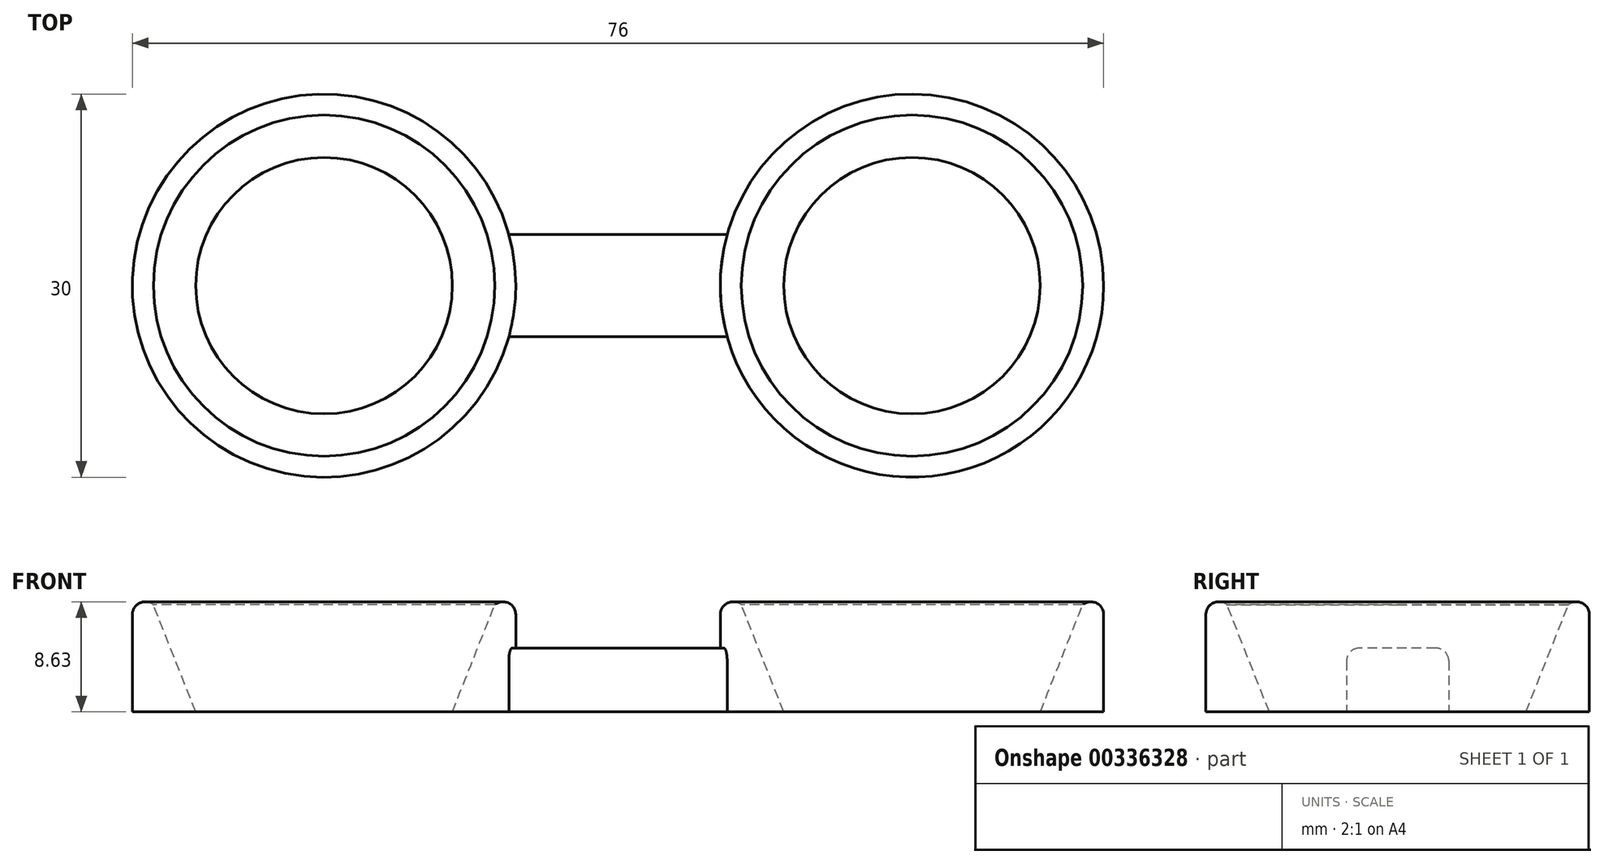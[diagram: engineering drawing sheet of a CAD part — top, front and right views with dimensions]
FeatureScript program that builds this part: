
annotation { "Feature Type Name" : "Feature", "Feature Type Description" : "" }
export const myFeature = defineFeature(function(context is Context, id is Id, definition is map)
    precondition{}
    {
        {
            var Q0;
            Q0=qCreatedBy(makeId("Top.planeOp"),FACE);
            var sketch = newSketch(context, id + "F0", { "sketchPlane" : qUnion([Q0])});
            skLineSegment(sketch, "E0", {"start": v(-23, 0) * mm, "end": v(23, 0) * mm, "construction": true});
            skPoint(sketch, "E1", {"position": v(0, 0) * mm});
            skCircle(sketch, "E2", {"center": v(-23, 0) * mm, "radius": 15 * mm});
            skCircle(sketch, "E3", {"center": v(23, 0) * mm, "radius": 15 * mm});
            skLineSegment(sketch, "E4", {"start": v(0, 0) * mm, "end": v(0, 4) * mm, "construction": true});
            skLineSegment(sketch, "E5", {"start": v(0, 0) * mm, "end": v(0, -4) * mm, "construction": true});
            skLineSegment(sketch, "E6", {"start": v(8.54, -4) * mm, "end": v(-8.54, -4) * mm});
            skLineSegment(sketch, "E7", {"start": v(8.54, 4) * mm, "end": v(-8.54, 4) * mm});
            skSolve(sketch);
        }
        {
            var Q0;
            {var subQ0=sQuery(id+"F0.wireOp",EDGE,"E6");Q0=makeQuery(id+"F0.imprint","IMPRINT",FACE,{"disambiguationData":[TD([[makeQuery(id+"F0.imprint","IMPRINT",EDGE,{"derivedFrom":subQ0}),-1.0]])]});}
            extrude(context, id + "F1", {"entities" : qUnion([Q0]), "depth" : 5 * mm});
        }
        {
            var Q0;
            {var subQ0=sQuery(id+"F0.wireOp",EDGE,"E2");var subQ1=makeQuery(id+"F0.imprint","INTERSECT",VERTEX,{"derivedFrom":[subQ0,sQuery(id+"F0.wireOp",EDGE,"E6")]});Q0=makeQuery(id+"F0.imprint","IMPRINT",FACE,{"disambiguationData":[TD([[makeQuery(id+"F0.imprint","IMPRINT",EDGE,{"disambiguationData":[TD([[subQ1,1.0]])],"derivedFrom":subQ0}),1.0]])]});}
            var Q1;
            {var subQ0=sQuery(id+"F0.wireOp",EDGE,"E3");var subQ1=makeQuery(id+"F0.imprint","INTERSECT",VERTEX,{"derivedFrom":[subQ0,sQuery(id+"F0.wireOp",EDGE,"E6")]});Q1=makeQuery(id+"F0.imprint","IMPRINT",FACE,{"disambiguationData":[TD([[makeQuery(id+"F0.imprint","IMPRINT",EDGE,{"disambiguationData":[TD([[subQ1,1.0]])],"derivedFrom":subQ0}),1.0]])]});}
            extrude(context, id + "F2", {"entities" : qUnion([Q0, Q1]), "operationType" : NewBodyOperationType.ADD, "depth" : 10 * mm});
        }
        {
            var Q0;
            Q0=qCreatedBy(makeId("Front.planeOp"),FACE);
            var sketch = newSketch(context, id + "F3", { "sketchPlane" : qUnion([Q0])});
            skLineSegment(sketch, "E8", {"start": v(-23, 0) * mm, "end": v(23, 0) * mm, "construction": true});
            skPoint(sketch, "E9", {"position": v(0, 0) * mm});
            skLineSegment(sketch, "E10", {"start": v(-23, 0) * mm, "end": v(-23, 26.5) * mm, "construction": true});
            skLineSegment(sketch, "E11", {"start": v(23, 0) * mm, "end": v(23, 26.5) * mm, "construction": true});
            skArc(sketch, "E12", {"start": v(-23, 49) * mm, "mid": v(-45.5, 26.5) * mm, "end": v(-23, 4) * mm});
            skArc(sketch, "E13", {"start": v(23, 49) * mm, "mid": v(0.5, 26.5) * mm, "end": v(23, 4) * mm});
            skLineSegment(sketch, "E14", {"start": v(-23, 49) * mm, "end": v(-23, 4) * mm});
            skLineSegment(sketch, "E15", {"start": v(23, 4) * mm, "end": v(23, 49) * mm});
            skSolve(sketch);
        }
        {
            var Q0;
            Q0=makeQuery(id+"F3.imprint","IMPRINT",FACE,{"disambiguationData":[TD([[makeQuery(id+"F3.imprint","IMPRINT",EDGE,{"derivedFrom":sQuery(id+"F3.wireOp",EDGE,"E12")}),1.0]])]});
            var Q1;
            Q1=sQuery(id+"F3.wireOp",EDGE,"E10");
            revolve(context, id + "F4", {"operationType" : NewBodyOperationType.REMOVE, "entities" : qUnion([Q0]), "axis" : qUnion([Q1]), "revolveType" : RevolveType.FULL, "oppositeDirection" : true});
        }
        {
            var Q0;
            Q0=makeQuery(id+"F3.imprint","IMPRINT",FACE,{"disambiguationData":[TD([[makeQuery(id+"F3.imprint","IMPRINT",EDGE,{"derivedFrom":sQuery(id+"F3.wireOp",EDGE,"E13")}),1.0]])]});
            var Q1;
            Q1=sQuery(id+"F3.wireOp",EDGE,"E11");
            revolve(context, id + "F5", {"operationType" : NewBodyOperationType.REMOVE, "entities" : qUnion([Q0]), "axis" : qUnion([Q1]), "revolveType" : RevolveType.FULL});
        }
        {
            var Q0;
            Q0=makeQuery(id+"F4.boolean.opBoolean","INTERSECT",EDGE,{"derivedFrom":[makeQuery(id+"F2.opExtrude","SWEPT_FACE",FACE,{"disambiguationData":[OSD([sQuery(id+"F0.wireOp",EDGE,"E2")])]}),makeQuery(id+"F4.opRevolve","SWEPT_FACE",FACE,{"disambiguationData":[OSD([sQuery(id+"F3.wireOp",EDGE,"E12")])]})]});
            var Q1;
            Q1=makeQuery(id+"F5.boolean.opBoolean","INTERSECT",EDGE,{"derivedFrom":[makeQuery(id+"F2.opExtrude","SWEPT_FACE",FACE,{"disambiguationData":[OSD([sQuery(id+"F0.wireOp",EDGE,"E3")])]}),makeQuery(id+"F5.opRevolve","SWEPT_FACE",FACE,{"disambiguationData":[OSD([sQuery(id+"F3.wireOp",EDGE,"E13")])]})]});
            var Q2;
            Q2=makeQuery(id+"F1.opExtrude","CAP_EDGE",EDGE,{"disambiguationData":[OSD([sQuery(id+"F0.wireOp",EDGE,"E6")])],"isStart":false});
            var Q3;
            Q3=makeQuery(id+"F1.opExtrude","CAP_EDGE",EDGE,{"disambiguationData":[OSD([sQuery(id+"F0.wireOp",EDGE,"E7")])],"isStart":false});
            var Q4;
            Q4=makeQuery(id+"F1.opExtrude","CAP_EDGE",EDGE,{"disambiguationData":[OSD([sQuery(id+"F0.wireOp",EDGE,"E2")])],"isStart":false});
            var Q5;
            Q5=makeQuery(id+"F1.opExtrude","CAP_EDGE",EDGE,{"disambiguationData":[OSD([sQuery(id+"F0.wireOp",EDGE,"E3")])],"isStart":false});
            fillet(context, id + "F6", {"entities" : qUnion([Q0, Q1, Q2, Q3, Q4, Q5]), "radius" : 1 * mm, "tangentPropagation" : true, "allowEdgeOverflow" : false});
        }
        {
            var Q0;
            Q0=qCreatedBy(makeId("Top.planeOp"),FACE);
            cPlane(context, id + "F7", {"entities" : qUnion([Q0]), "cplaneType" : CPlaneType.OFFSET, "offset" : 20 * mm, "width" : 150 * mm, "height" : 150 * mm});
        }
        {
            var Q0;
            Q0=qCreatedBy(id+"F7.planeOp",FACE);
            var sketch = newSketch(context, id + "F8", { "sketchPlane" : qUnion([Q0])});
            skLineSegment(sketch, "E16", {"start": v(-23, 0) * mm, "end": v(23, 0) * mm, "construction": true});
            skPoint(sketch, "E17", {"position": v(0, 0) * mm});
            skCircle(sketch, "E18", {"center": v(-23, 0) * mm, "radius": 10 * mm});
            skCircle(sketch, "E19", {"center": v(23, 0) * mm, "radius": 10 * mm});
            skSolve(sketch);
        }
        {
            var Q0;
            Q0=makeQuery(id+"F8.imprint","IMPRINT",FACE,{"disambiguationData":[TD([[makeQuery(id+"F8.imprint","IMPRINT",EDGE,{"derivedFrom":sQuery(id+"F8.wireOp",EDGE,"E18")}),1.0]])]});
            var Q1;
            Q1=makeQuery(id+"F8.imprint","IMPRINT",FACE,{"disambiguationData":[TD([[makeQuery(id+"F8.imprint","IMPRINT",EDGE,{"derivedFrom":sQuery(id+"F8.wireOp",EDGE,"E19")}),1.0]])]});
            extrude(context, id + "F9", {"entities" : qUnion([Q0, Q1]), "operationType" : NewBodyOperationType.REMOVE, "oppositeDirection" : true, "depth" : 25 * mm});
        }
        {
            var Q0;
            Q0=makeQuery(id+"F9.boolean.opBoolean","INTERSECT",EDGE,{"derivedFrom":[makeQuery(id+"F4.boolean.opBoolean","COPY",FACE,{"derivedFrom":makeQuery(id+"F4.opRevolve","SWEPT_FACE",FACE,{"disambiguationData":[OSD([sQuery(id+"F3.wireOp",EDGE,"E12")])]})}),makeQuery(id+"F9.opExtrude","SWEPT_FACE",FACE,{"disambiguationData":[OSD([sQuery(id+"F8.wireOp",EDGE,"E18")])]})]});
            chamfer(context, id + "F10", {"entities" : qUnion([Q0]), "chamferType" : ChamferType.TWO_OFFSETS, "width1" : 5.5 * mm, "oppositeDirection" : false, "width2" : 7 * mm, "tangentPropagation" : true});
        }
        {
            var Q0;
            Q0=makeQuery(id+"F9.boolean.opBoolean","INTERSECT",EDGE,{"derivedFrom":[makeQuery(id+"F5.boolean.opBoolean","COPY",FACE,{"derivedFrom":makeQuery(id+"F5.opRevolve","SWEPT_FACE",FACE,{"disambiguationData":[OSD([sQuery(id+"F3.wireOp",EDGE,"E13")])]})}),makeQuery(id+"F9.opExtrude","SWEPT_FACE",FACE,{"disambiguationData":[OSD([sQuery(id+"F8.wireOp",EDGE,"E19")])]})]});
            chamfer(context, id + "F11", {"entities" : qUnion([Q0]), "chamferType" : ChamferType.TWO_OFFSETS, "width1" : 7 * mm, "oppositeDirection" : false, "width2" : 5.5 * mm, "tangentPropagation" : true});
        }
    });
